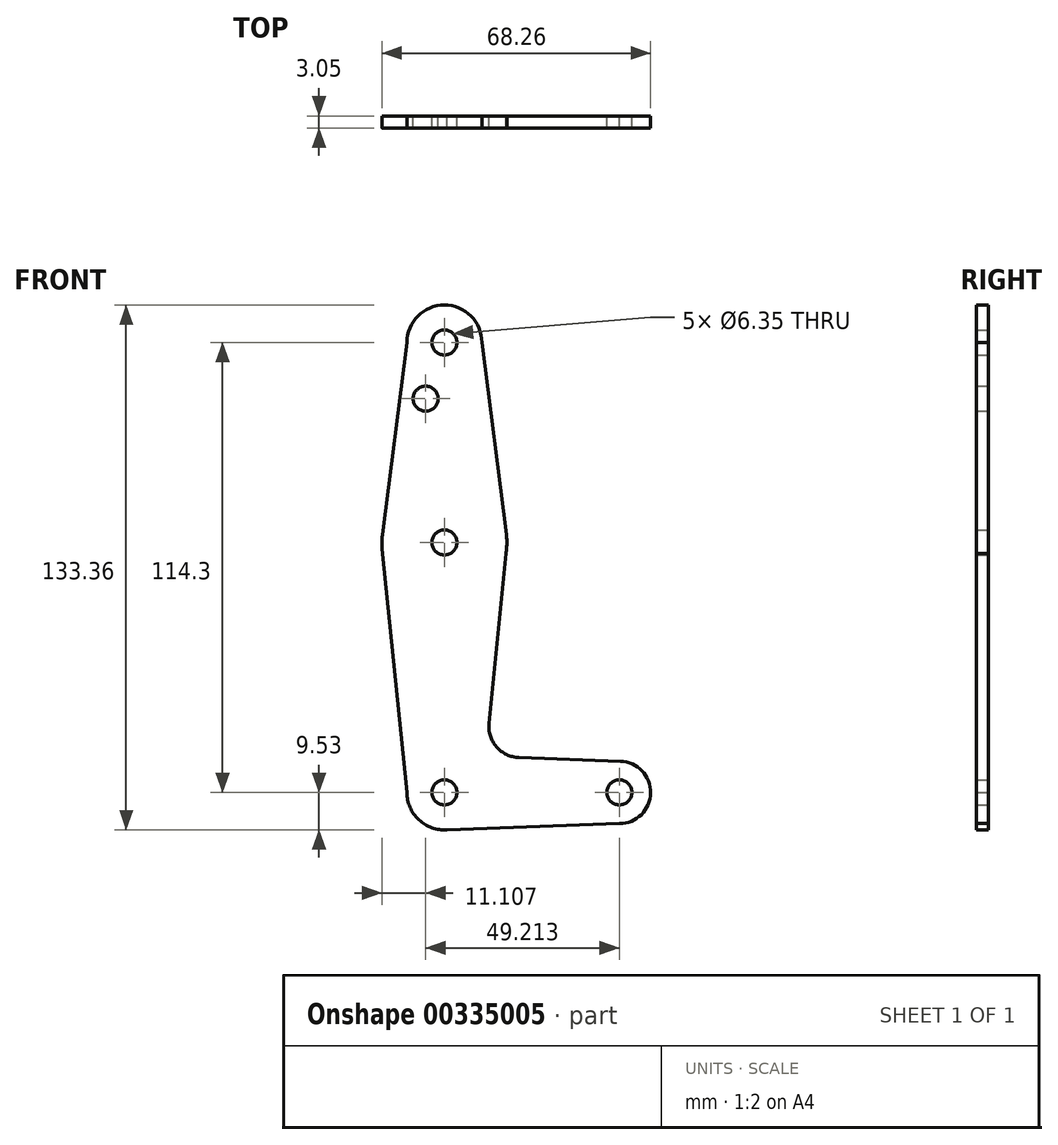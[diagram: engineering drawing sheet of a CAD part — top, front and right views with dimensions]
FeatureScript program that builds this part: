
annotation { "Feature Type Name" : "Feature", "Feature Type Description" : "" }
export const myFeature = defineFeature(function(context is Context, id is Id, definition is map)
    precondition{}
    {
        {
            var Q0;
            Q0=qCreatedBy(makeId("Front.planeOp"),FACE);
            var sketch = newSketch(context, id + "F0", { "sketchPlane" : qUnion([Q0])});
            skLineSegment(sketch, "E0", {"start": v(0, 0) * mm, "end": v(0, 114.3) * mm, "construction": true});
            skLineSegment(sketch, "E1", {"start": v(0, 0) * mm, "end": v(44.45, 0) * mm});
            skCircle(sketch, "E2", {"center": v(0, 63.5) * mm, "radius": 15.88 * mm});
            skCircle(sketch, "E3", {"center": v(0, 0) * mm, "radius": 9.53 * mm});
            skCircle(sketch, "E4", {"center": v(44.45, 0) * mm, "radius": 7.94 * mm});
            skCircle(sketch, "E5", {"center": v(0, 114.3) * mm, "radius": 9.53 * mm});
            skLineSegment(sketch, "E6", {"start": v(-9.53, 114.3) * mm, "end": v(-15.75, 65.5) * mm});
            skLineSegment(sketch, "E7", {"start": v(9.53, 114.3) * mm, "end": v(15.75, 65.5) * mm});
            skLineSegment(sketch, "E8", {"start": v(-9.53, 0) * mm, "end": v(-15.8, 61.9) * mm});
            skLineSegment(sketch, "E9", {"start": v(15.75, 61.9) * mm, "end": v(11.33, 17.58) * mm});
            skLineSegment(sketch, "E10", {"start": v(0, -9.52) * mm, "end": v(44.45, -7.94) * mm});
            skLineSegment(sketch, "E11", {"start": v(18.95, 8.85) * mm, "end": v(44.73, 7.93) * mm});
            skCircle(sketch, "E12", {"center": v(-4.76, 100.03) * mm, "radius": 3.18 * mm});
            skPoint(sketch, "E13.newPointA", {"position": v(9.57, 0) * mm});
            skPoint(sketch, "E13.newPointB", {"position": v(0, 9.53) * mm});
            skArc(sketch, "E13.filletArc", {"start": v(11.33, 17.58) * mm, "mid": v(13.25, 11.57) * mm, "end": v(18.95, 8.85) * mm});
            skCircle(sketch, "E14", {"center": v(0, 114.3) * mm, "radius": 3.18 * mm});
            skCircle(sketch, "E15", {"center": v(0, 63.5) * mm, "radius": 3.18 * mm});
            skCircle(sketch, "E16", {"center": v(0, 0) * mm, "radius": 3.18 * mm});
            skCircle(sketch, "E17", {"center": v(44.45, 0) * mm, "radius": 3.18 * mm});
            skSolve(sketch);
        }
        {
            var Q0;
            Q0 = qSketchRegion(id + "F0", true);
            extrude(context, id + "F1", {"entities" : qUnion([Q0]), "depth" : 3.05 * mm});
        }
    });
